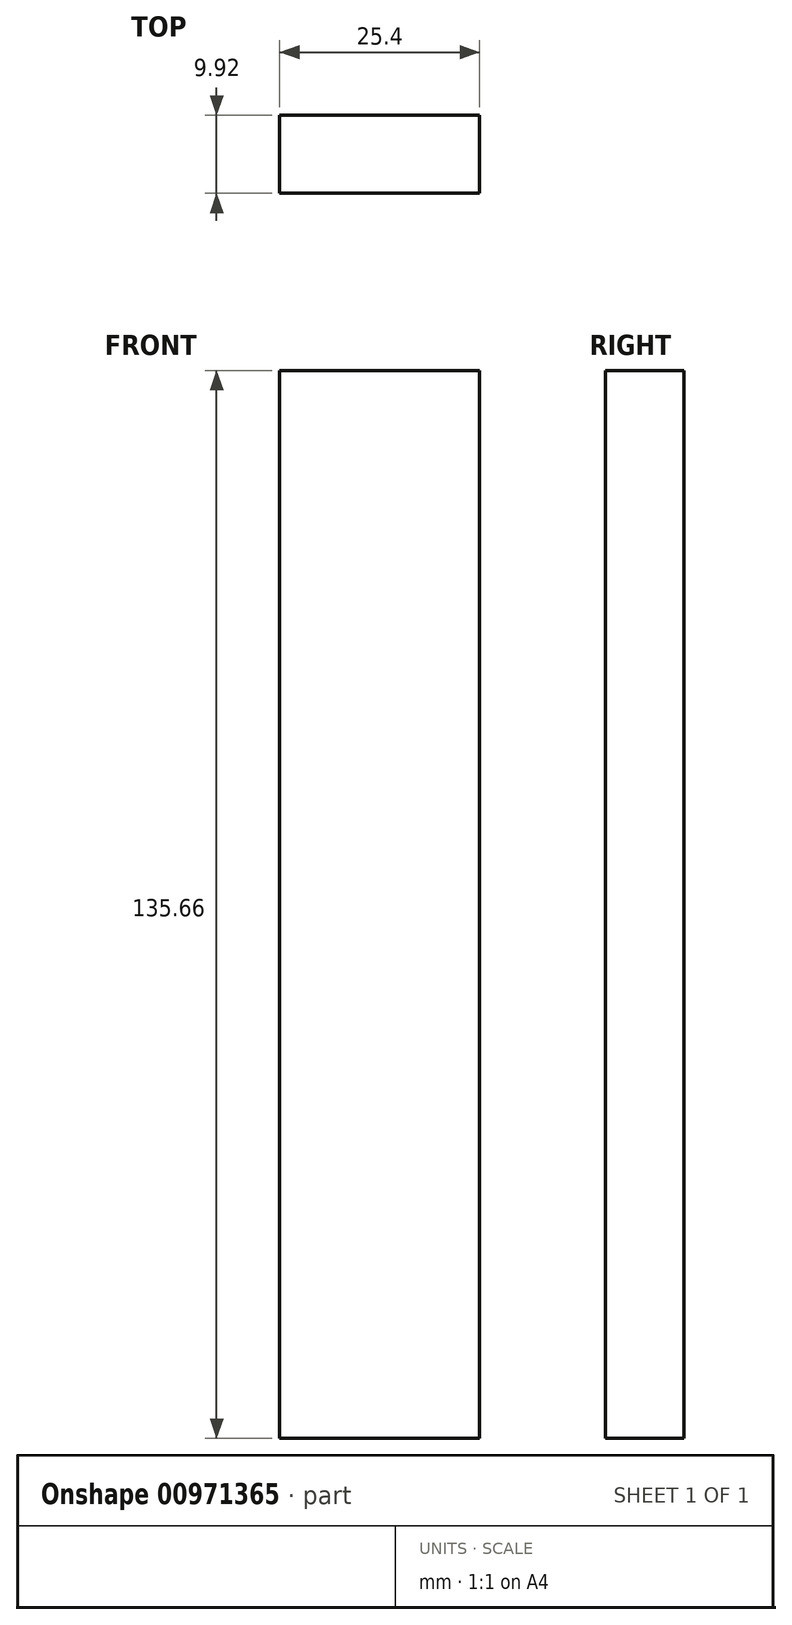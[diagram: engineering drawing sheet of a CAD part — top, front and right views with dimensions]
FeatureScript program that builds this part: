
annotation { "Feature Type Name" : "Feature", "Feature Type Description" : "" }
export const myFeature = defineFeature(function(context is Context, id is Id, definition is map)
    precondition{}
    {
        {
            var Q0;
            Q0=qCreatedBy(makeId("Right.planeOp"),FACE);
            var sketch = newSketch(context, id + "F0", { "sketchPlane" : qUnion([Q0])});
            skLineSegment(sketch, "E0.bottom", {"start": v(4.96, 67.83) * mm, "end": v(-4.96, 67.83) * mm});
            skLineSegment(sketch, "E0.top", {"start": v(4.96, -67.83) * mm, "end": v(-4.96, -67.83) * mm});
            skLineSegment(sketch, "E0.left", {"start": v(4.96, 67.83) * mm, "end": v(4.96, -67.83) * mm});
            skLineSegment(sketch, "E0.right", {"start": v(-4.96, 67.83) * mm, "end": v(-4.96, -67.83) * mm});
            skPoint(sketch, "E0.middle", {"position": v(0, 0) * mm});
            skSolve(sketch);
        }
        {
            var Q0;
            Q0=makeQuery(id+"F0.imprint","IMPRINT",FACE,{"disambiguationData":[TD([[makeQuery(id+"F0.imprint","IMPRINT",EDGE,{"derivedFrom":sQuery(id+"F0.wireOp",EDGE,"E0.bottom")}),1.0]])]});
            extrude(context, id + "F1", {"entities" : qUnion([Q0]), "depth" : 25.4 * mm, "offsetDistance" : 25.4 * mm});
        }
    });
